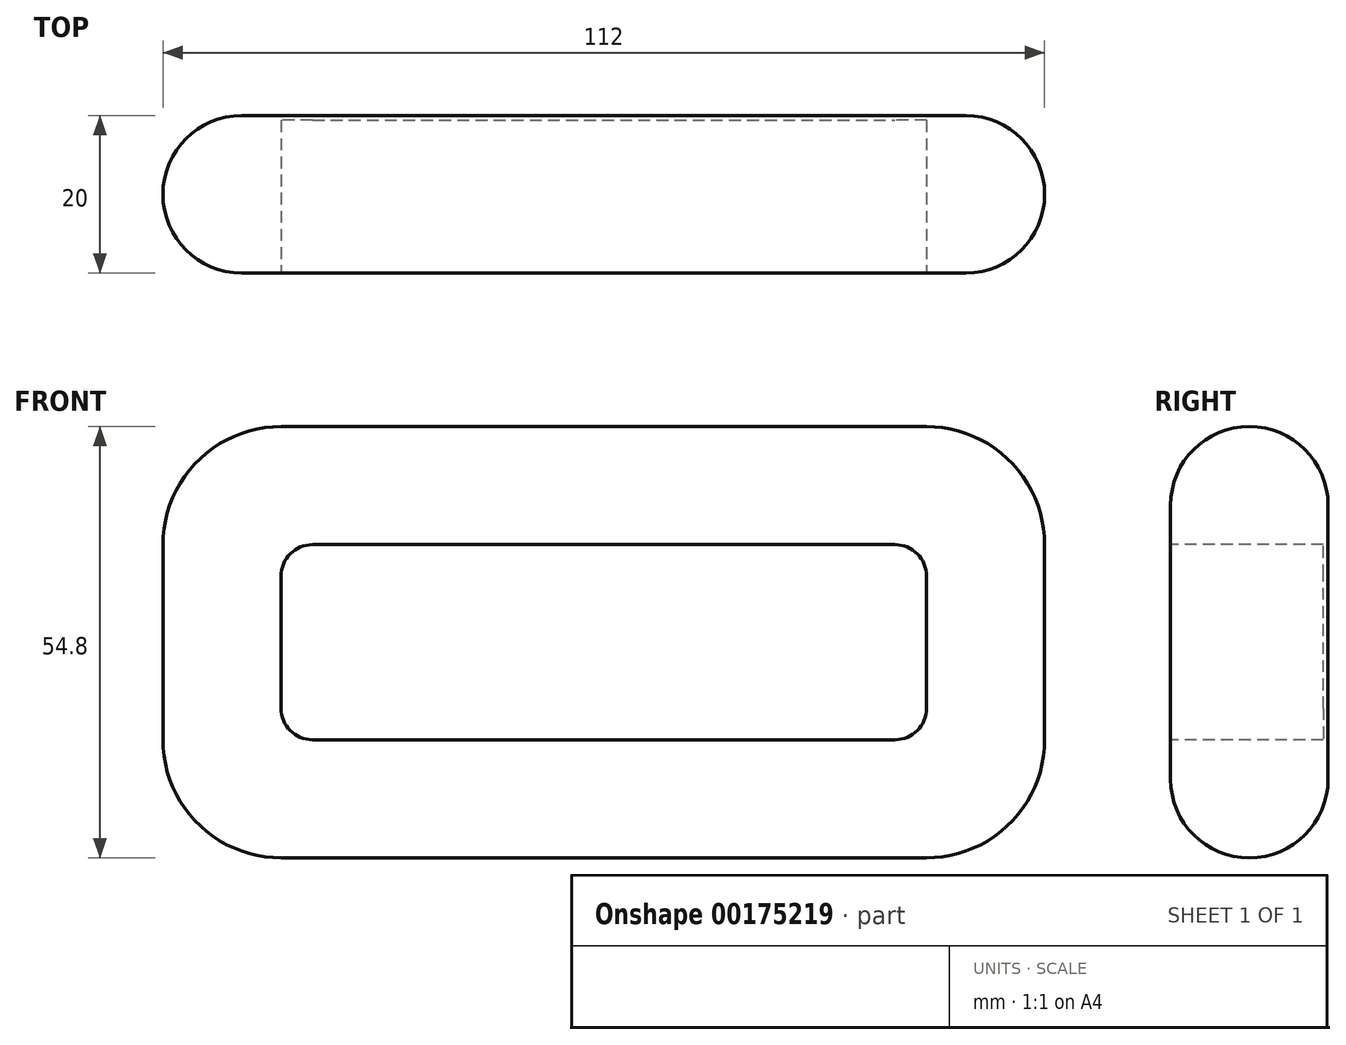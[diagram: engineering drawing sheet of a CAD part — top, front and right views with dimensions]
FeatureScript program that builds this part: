
annotation { "Feature Type Name" : "Feature", "Feature Type Description" : "" }
export const myFeature = defineFeature(function(context is Context, id is Id, definition is map)
    precondition{}
    {
        {
            var Q0;
            Q0=qCreatedBy(makeId("Front.planeOp"),FACE);
            var sketch = newSketch(context, id + "F0", { "sketchPlane" : qUnion([Q0])});
            skLineSegment(sketch, "E0.bottom", {"start": v(41, 27.4) * mm, "end": v(-41, 27.4) * mm});
            skLineSegment(sketch, "E0.top", {"start": v(41, -27.4) * mm, "end": v(-41, -27.4) * mm});
            skLineSegment(sketch, "E0.left", {"start": v(56, 12.4) * mm, "end": v(56, -12.4) * mm});
            skLineSegment(sketch, "E0.right", {"start": v(-56, 12.4) * mm, "end": v(-56, -12.4) * mm});
            skPoint(sketch, "E0.middle", {"position": v(0, 0) * mm});
            skPoint(sketch, "E1.visualSharp", {"position": v(-56, 27.4) * mm});
            skArc(sketch, "E1.filletArc", {"start": v(-41, 27.4) * mm, "mid": v(-51.6, 23) * mm, "end": v(-56, 12.4) * mm});
            skPoint(sketch, "E2.visualSharp", {"position": v(56, 27.4) * mm});
            skArc(sketch, "E2.filletArc", {"start": v(56, 12.4) * mm, "mid": v(51.6, 23) * mm, "end": v(41, 27.4) * mm});
            skPoint(sketch, "E3.visualSharp", {"position": v(56, -27.4) * mm});
            skArc(sketch, "E3.filletArc", {"start": v(41, -27.4) * mm, "mid": v(51.6, -23) * mm, "end": v(56, -12.4) * mm});
            skPoint(sketch, "E4.visualSharp", {"position": v(-56, -27.4) * mm});
            skArc(sketch, "E4.filletArc", {"start": v(-56, -12.4) * mm, "mid": v(-51.6, -23) * mm, "end": v(-41, -27.4) * mm});
            skSolve(sketch);
        }
        {
            var Q0;
            Q0=makeQuery(id+"F0.imprint","IMPRINT",FACE,{"disambiguationData":[TD([[makeQuery(id+"F0.imprint","IMPRINT",EDGE,{"derivedFrom":sQuery(id+"F0.wireOp",EDGE,"E0.bottom")}),1.0]])]});
            extrude(context, id + "F1", {"entities" : qUnion([Q0]), "depth" : 20 * mm});
        }
        {
            var Q0;
            Q0=makeQuery(id+"F1.opExtrude","CAP_FACE",FACE,{"disambiguationData":[OSD([sQuery(id+"F0.wireOp",EDGE,"E0.bottom"),sQuery(id+"F0.wireOp",EDGE,"E0.top"),sQuery(id+"F0.wireOp",EDGE,"E0.left"),sQuery(id+"F0.wireOp",EDGE,"E0.right"),sQuery(id+"F0.wireOp",EDGE,"E1.filletArc"),sQuery(id+"F0.wireOp",EDGE,"E2.filletArc"),sQuery(id+"F0.wireOp",EDGE,"E3.filletArc"),sQuery(id+"F0.wireOp",EDGE,"E4.filletArc")])],"isStart":false});
            var Q1;
            Q1=makeQuery(id+"F1.opExtrude","CAP_EDGE",EDGE,{"disambiguationData":[OSD([sQuery(id+"F0.wireOp",EDGE,"E0.bottom")])],"isStart":true});
            fillet(context, id + "F2", {"entities" : qUnion([Q0, Q1]), "radius" : 10 * mm, "tangentPropagation" : true, "allowEdgeOverflow" : false});
        }
        {
            var Q0;
            Q0=makeQuery(id+"F1.opExtrude","CAP_FACE",FACE,{"disambiguationData":[OSD([sQuery(id+"F0.wireOp",EDGE,"E0.bottom"),sQuery(id+"F0.wireOp",EDGE,"E0.top"),sQuery(id+"F0.wireOp",EDGE,"E0.left"),sQuery(id+"F0.wireOp",EDGE,"E0.right"),sQuery(id+"F0.wireOp",EDGE,"E1.filletArc"),sQuery(id+"F0.wireOp",EDGE,"E2.filletArc"),sQuery(id+"F0.wireOp",EDGE,"E3.filletArc"),sQuery(id+"F0.wireOp",EDGE,"E4.filletArc")])],"isStart":false});
            var sketch = newSketch(context, id + "F3", { "sketchPlane" : qUnion([Q0])});
            skLineSegment(sketch, "E5.bottom", {"start": v(-37, -12.4) * mm, "end": v(37, -12.4) * mm});
            skLineSegment(sketch, "E5.top", {"start": v(-37, 12.4) * mm, "end": v(37, 12.4) * mm});
            skLineSegment(sketch, "E5.left", {"start": v(-41, -8.4) * mm, "end": v(-41, 8.4) * mm});
            skLineSegment(sketch, "E5.right", {"start": v(41, -8.4) * mm, "end": v(41, 8.4) * mm});
            skPoint(sketch, "E5.middle", {"position": v(0, 0) * mm});
            skPoint(sketch, "E6.visualSharp", {"position": v(-41, 12.4) * mm});
            skArc(sketch, "E6.filletArc", {"start": v(-37, 12.4) * mm, "mid": v(-39.83, 11.23) * mm, "end": v(-41, 8.4) * mm});
            skPoint(sketch, "E7.visualSharp", {"position": v(41, 12.4) * mm});
            skArc(sketch, "E7.filletArc", {"start": v(41, 8.4) * mm, "mid": v(39.83, 11.23) * mm, "end": v(37, 12.4) * mm});
            skPoint(sketch, "E8.visualSharp", {"position": v(41, -12.4) * mm});
            skArc(sketch, "E8.filletArc", {"start": v(37, -12.4) * mm, "mid": v(39.83, -11.23) * mm, "end": v(41, -8.4) * mm});
            skPoint(sketch, "E9.visualSharp", {"position": v(-41, -12.4) * mm});
            skArc(sketch, "E9.filletArc", {"start": v(-41, -8.4) * mm, "mid": v(-39.83, -11.23) * mm, "end": v(-37, -12.4) * mm});
            skSolve(sketch);
        }
        {
            var Q0;
            Q0=makeQuery(id+"F3.imprint","IMPRINT",FACE,{"disambiguationData":[TD([[makeQuery(id+"F3.imprint","IMPRINT",EDGE,{"derivedFrom":sQuery(id+"F3.wireOp",EDGE,"E5.bottom")}),1.0]])]});
            extrude(context, id + "F4", {"entities" : qUnion([Q0]), "operationType" : NewBodyOperationType.REMOVE, "oppositeDirection" : true, "depth" : 19.4 * mm});
        }
    });
